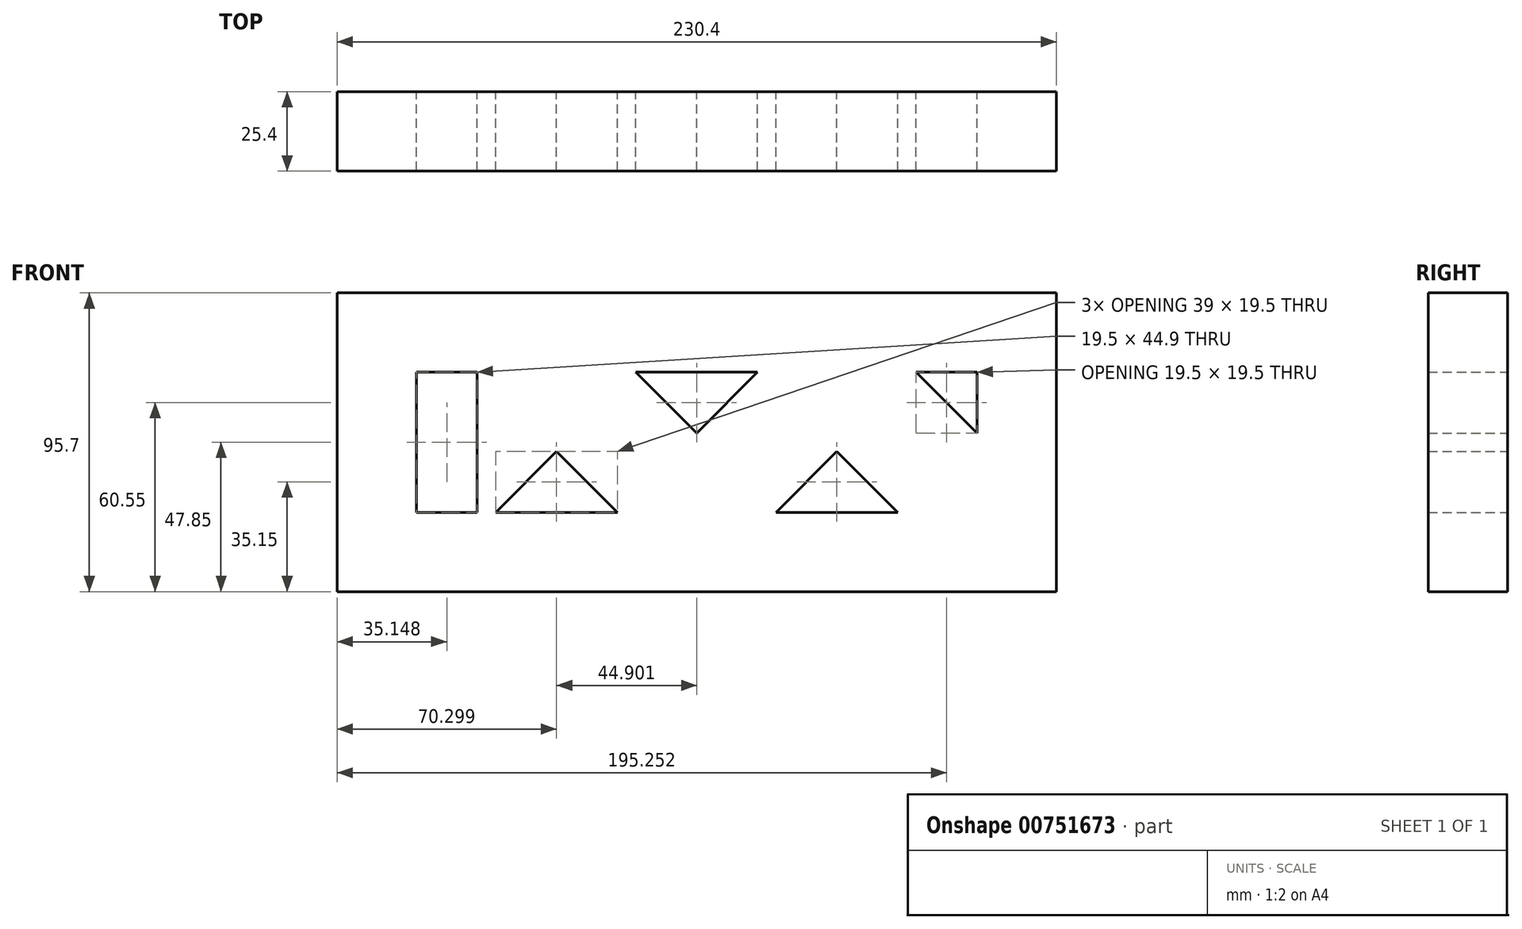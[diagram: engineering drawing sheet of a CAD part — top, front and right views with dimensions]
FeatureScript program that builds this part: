
annotation { "Feature Type Name" : "Feature", "Feature Type Description" : "" }
export const myFeature = defineFeature(function(context is Context, id is Id, definition is map)
    precondition{}
    {
        {
            var Q0;
            Q0=qCreatedBy(makeId("Front.planeOp"),FACE);
            var sketch = newSketch(context, id + "F0", { "sketchPlane" : qUnion([Q0])});
            skLineSegment(sketch, "E0", {"start": v(-89.8, -22.45) * mm, "end": v(-64.4, -22.45) * mm});
            skLineSegment(sketch, "E1", {"start": v(-64.4, -22.45) * mm, "end": v(-44.9, -2.95) * mm});
            skLineSegment(sketch, "E2", {"start": v(-44.9, -2.95) * mm, "end": v(-44.9, 22.45) * mm});
            skLineSegment(sketch, "E3", {"start": v(-44.9, 22.45) * mm, "end": v(-70.3, 22.45) * mm});
            skLineSegment(sketch, "E4", {"start": v(-70.3, 22.45) * mm, "end": v(-89.8, 2.95) * mm});
            skLineSegment(sketch, "E5", {"start": v(-89.8, 2.95) * mm, "end": v(-89.8, -22.45) * mm});
            skLineSegment(sketch, "E6", {"start": v(-89.8, -22.45) * mm, "end": v(-44.9, 22.45) * mm, "construction": true});
            skLineSegment(sketch, "E7", {"start": v(0, -22.45) * mm, "end": v(0, 2.95) * mm});
            skLineSegment(sketch, "E8", {"start": v(0, 2.95) * mm, "end": v(-19.5, 22.45) * mm});
            skLineSegment(sketch, "E9", {"start": v(-19.5, 22.45) * mm, "end": v(-44.9, 22.45) * mm});
            skLineSegment(sketch, "E10", {"start": v(-44.9, 22.45) * mm, "end": v(-44.9, -2.95) * mm});
            skLineSegment(sketch, "E11", {"start": v(-44.9, -2.95) * mm, "end": v(-25.4, -22.45) * mm});
            skLineSegment(sketch, "E12", {"start": v(-25.4, -22.45) * mm, "end": v(0, -22.45) * mm});
            skLineSegment(sketch, "E13", {"start": v(0, -22.45) * mm, "end": v(-44.9, 22.45) * mm, "construction": true});
            skLineSegment(sketch, "E14", {"start": v(0, -22.45) * mm, "end": v(25.4, -22.45) * mm});
            skLineSegment(sketch, "E15", {"start": v(25.4, -22.45) * mm, "end": v(44.9, -2.95) * mm});
            skLineSegment(sketch, "E16", {"start": v(44.9, -2.95) * mm, "end": v(44.9, 22.45) * mm});
            skLineSegment(sketch, "E17", {"start": v(44.9, 22.45) * mm, "end": v(19.5, 22.45) * mm});
            skLineSegment(sketch, "E18", {"start": v(19.5, 22.45) * mm, "end": v(0, 2.95) * mm});
            skLineSegment(sketch, "E19", {"start": v(0, 2.95) * mm, "end": v(0, -22.45) * mm});
            skLineSegment(sketch, "E20", {"start": v(0, -22.45) * mm, "end": v(44.9, 22.45) * mm, "construction": true});
            skLineSegment(sketch, "E21", {"start": v(89.8, -22.45) * mm, "end": v(89.8, 2.95) * mm});
            skLineSegment(sketch, "E22", {"start": v(89.8, 2.95) * mm, "end": v(70.3, 22.45) * mm});
            skLineSegment(sketch, "E23", {"start": v(70.3, 22.45) * mm, "end": v(44.9, 22.45) * mm});
            skLineSegment(sketch, "E24", {"start": v(44.9, 22.45) * mm, "end": v(44.9, -2.95) * mm});
            skLineSegment(sketch, "E25", {"start": v(44.9, -2.95) * mm, "end": v(64.4, -22.45) * mm});
            skLineSegment(sketch, "E26", {"start": v(64.4, -22.45) * mm, "end": v(89.8, -22.45) * mm});
            skLineSegment(sketch, "E27", {"start": v(89.8, -22.45) * mm, "end": v(44.9, 22.45) * mm, "construction": true});
            skLineSegment(sketch, "E28.bottom", {"start": v(89.8, 22.45) * mm, "end": v(-89.8, 22.45) * mm});
            skLineSegment(sketch, "E28.top", {"start": v(89.8, -22.45) * mm, "end": v(-89.8, -22.45) * mm});
            skLineSegment(sketch, "E28.left", {"start": v(89.8, 22.45) * mm, "end": v(89.8, -22.45) * mm});
            skLineSegment(sketch, "E28.right", {"start": v(-89.8, 22.45) * mm, "end": v(-89.8, -22.45) * mm});
            skPoint(sketch, "E28.middle", {"position": v(0, 0) * mm});
            skLineSegment(sketch, "E29", {"start": v(0, 22.45) * mm, "end": v(0, -22.45) * mm, "construction": true});
            skLineSegment(sketch, "E30", {"start": v(-89.8, 22.45) * mm, "end": v(0, 22.45) * mm, "construction": true});
            skLineSegment(sketch, "E31", {"start": v(-44.9, 22.45) * mm, "end": v(-44.9, -22.45) * mm, "construction": true});
            skLineSegment(sketch, "E32", {"start": v(-89.8, 2.95) * mm, "end": v(-89.8, -22.45) * mm, "construction": true});
            skLineSegment(sketch, "E33.bottom", {"start": v(115.2, 47.85) * mm, "end": v(-115.2, 47.85) * mm});
            skLineSegment(sketch, "E33.top", {"start": v(115.2, -47.85) * mm, "end": v(-115.2, -47.85) * mm});
            skLineSegment(sketch, "E33.left", {"start": v(115.2, 47.85) * mm, "end": v(115.2, -47.85) * mm});
            skLineSegment(sketch, "E33.right", {"start": v(-115.2, 47.85) * mm, "end": v(-115.2, -47.85) * mm});
            skLineSegment(sketch, "E34", {"start": v(-89.8, -22.45) * mm, "end": v(-89.8, -47.85) * mm, "construction": true});
            skLineSegment(sketch, "E35", {"start": v(-115.2, -47.85) * mm, "end": v(-89.8, -47.85) * mm, "construction": true});
            skLineSegment(sketch, "E36", {"start": v(-70.3, 22.45) * mm, "end": v(-70.3, -28.35) * mm});
            skSolve(sketch);
        }
        {
            var Q0;
            Q0=makeQuery(id+"F0.imprint","IMPRINT",FACE,{"disambiguationData":[TD([[makeQuery(id+"F0.imprint","IMPRINT",EDGE,{"derivedFrom":sQuery(id+"F0.wireOp",EDGE,"E33.bottom")}),1.0]])]});
            var Q1;
            {var subQ6=sQuery(id+"F0.wireOp",EDGE,"E1");Q1=makeQuery(id+"F0.imprint","IMPRINT",FACE,{"disambiguationData":[TD([[makeQuery(id+"F0.imprint","IMPRINT",EDGE,{"derivedFrom":subQ6}),1.0]])]});}
            var Q2;
            {var subQ2=sQuery(id+"F0.wireOp",EDGE,"E8");Q2=makeQuery(id+"F0.imprint","IMPRINT",FACE,{"disambiguationData":[TD([[makeQuery(id+"F0.imprint","IMPRINT",EDGE,{"derivedFrom":subQ2}),1.0]])]});}
            var Q3;
            {var subQ2=sQuery(id+"F0.wireOp",EDGE,"E15");Q3=makeQuery(id+"F0.imprint","IMPRINT",FACE,{"disambiguationData":[TD([[makeQuery(id+"F0.imprint","IMPRINT",EDGE,{"derivedFrom":subQ2}),1.0]])]});}
            var Q4;
            {var subQ1=sQuery(id+"F0.wireOp",EDGE,"E22");Q4=makeQuery(id+"F0.imprint","IMPRINT",FACE,{"disambiguationData":[TD([[makeQuery(id+"F0.imprint","IMPRINT",EDGE,{"derivedFrom":subQ1}),1.0]])]});}
            extrude(context, id + "F1", {"entities" : qUnion([Q0, Q1, Q2, Q3, Q4]), "depth" : 25.4 * mm, "offsetDistance" : 25.4 * mm});
        }
    });
